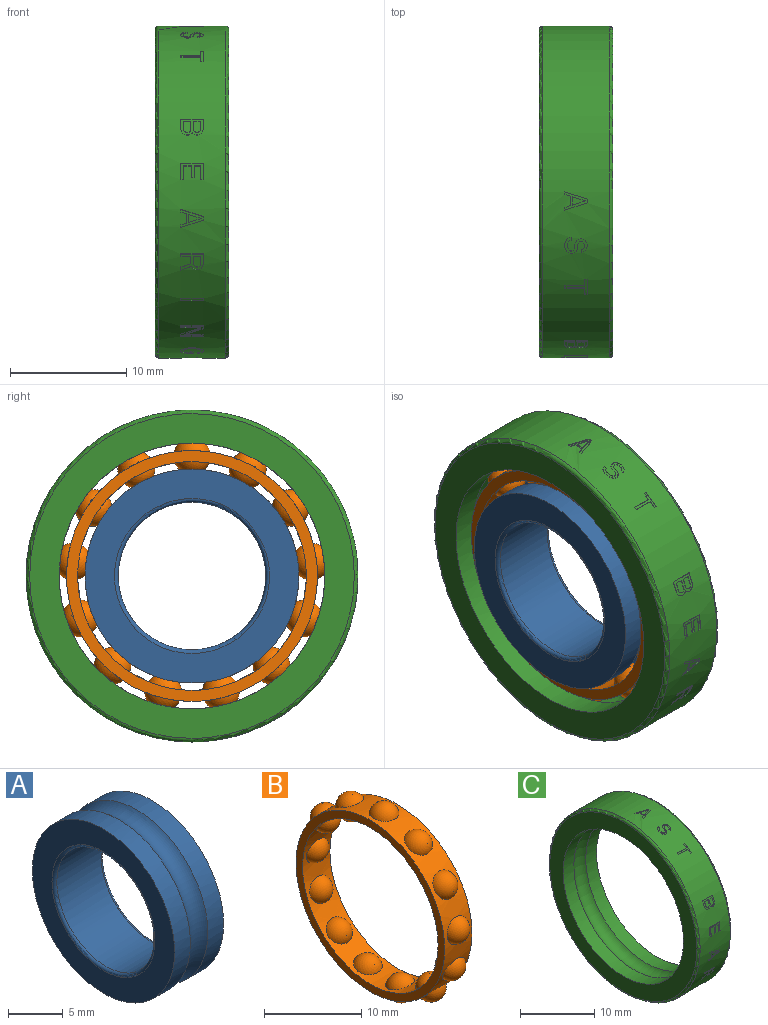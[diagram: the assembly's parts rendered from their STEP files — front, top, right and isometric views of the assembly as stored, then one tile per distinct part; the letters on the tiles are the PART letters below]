
ASSEMBLY  parts=3 mates=2
PART A: 8 faces, bbox 6.4x22.3x22.3 mm
  f0: torus R=10.32mm, axis (1,0,0), area 141.1mm2, adj f1,f2
  f1: cylinder r=9.21mm len=18.42mm, axis (1,0,0), area 118.1mm2, adj f0,f3
  f2: cylinder r=9.21mm len=18.42mm, axis (1,0,0), area 118.1mm2, adj f0,f4
  f3: plane 18.45x18.42mm, normal (-1,0,0), area 126.7mm2, adj f1,f5
  f4: plane 18.45x18.42mm, normal (1,0,0), area 126.7mm2, adj f2,f6
  f5: torus R=6.67mm, axis (1,0,0), area 20.3mm2, adj f3,f7
  f6: torus R=6.67mm, axis (1,0,0), area 20.3mm2, adj f4,f7
  f7: cylinder r=6.35mm len=12.7mm, axis (1,0,0), area 228mm2, adj f5,f6
PART B: 30 faces, bbox 4x23.7x23.5 mm
  f0: sphere r=1.59mm, area 11.9mm2, adj f13
  f1: sphere r=1.59mm, area 11.9mm2, adj f13
  f2: sphere r=1.59mm, area 12.1mm2, adj f13
  f3: sphere r=1.59mm, area 11.9mm2, adj f13
  f4: sphere r=1.59mm, area 12.1mm2, adj f13
  f5: sphere r=1.59mm, area 12.1mm2, adj f13
  f6: sphere r=1.59mm, area 14.4mm2, adj f13
  f7: sphere r=1.59mm, area 12.1mm2, adj f13
  f8: sphere r=1.59mm, area 11.9mm2, adj f13
  f9: sphere r=1.59mm, area 12.1mm2, adj f13
  f10: sphere r=1.59mm, area 12.1mm2, adj f13
  f11: sphere r=1.59mm, area 11.9mm2, adj f13
  f12: sphere r=1.59mm, area 11.5mm2, adj f13
  f13: cylinder r=10.79mm len=21.59mm, axis (1,0,0), area 173.7mm2, adj f0,f1,f2,f3,f4,f5,f6,f7
  f14: sphere r=1.59mm, area 10.5mm2, adj f28
  f15: sphere r=1.59mm, area 10.5mm2, adj f28
  f16: sphere r=1.59mm, area 10.5mm2, adj f28
  f17: sphere r=1.59mm, area 10.5mm2, adj f28
  f18: sphere r=1.59mm, area 10.5mm2, adj f28
  f19: sphere r=1.59mm, area 10.5mm2, adj f28
  f20: plane 21.61x21.59mm, normal (-1,0,0), area 61.8mm2, adj f13,f28
  f21: plane 21.61x21.59mm, normal (1,0,0), area 61.8mm2, adj f13,f28
  f22: sphere r=1.59mm, area 10.5mm2, adj f28
  f23: sphere r=1.59mm, area 10.5mm2, adj f28
  f24: sphere r=1.59mm, area 10.5mm2, adj f28
  f25: sphere r=1.59mm, area 10.5mm2, adj f28
  f26: sphere r=1.59mm, area 10.5mm2, adj f28
  f27: sphere r=1.59mm, area 10.5mm2, adj f28
  f28: cylinder r=9.84mm len=19.69mm, axis (1,0,0), area 153.1mm2, adj f14,f15,f16,f17,f18,f19,f20,f21
  f29: sphere r=1.59mm, area 10.5mm2, adj f28
PART C: 297 faces, bbox 6.4x30.9x30.9 mm
  f0: cylinder r=14.29mm len=1.09mm, axis (1,0,0), area 0.4mm2, adj f5,f6,f7
  f1: cylinder r=14.29mm len=0.91mm, axis (1,0,0), area 0.5mm2, adj f8,f9,f10,f11,f12,f13,f14,f15
  f2: cylinder r=14.29mm len=0.91mm, axis (1,0,0), area 0.6mm2, adj f18,f19,f20,f21,f22,f23,f24,f25
  f3: cylinder r=14.29mm len=1.09mm, axis (1,0,0), area 0.4mm2, adj f28,f29,f30
  f4: cylinder r=14.29mm len=0.9mm, axis (1,0,0), area 0.6mm2, adj f31,f32,f33,f34,f35,f36,f37,f38
  f5: plane 0.71x0.09mm, normal (-1,0,0), area 0mm2, adj f0,f6,f7,f41
  f6: plane 1.09x0.36mm, normal (0.31,0.95,0), area 0.1mm2, adj f0,f5,f7,f41
  f7: plane 1.09x0.36mm, normal (0.31,-0.95,0), area 0.1mm2, adj f0,f5,f6,f41
  f8: plane 0.13x0.09mm, normal (0.95,-0.14,-0.29), area 0mm2, adj f1,f9,f17,f45
  f9: plane 0.1x0.08mm, normal (0.7,-0.31,-0.64), area 0mm2, adj f1,f8,f10,f45
  f10: plane 0.12x0.06mm, normal (0.31,-0.42,-0.85), area 0mm2, adj f1,f9,f11,f45
  f11: plane 0.08x0.05mm, normal (0,-0.44,-0.9), area 0mm2, adj f1,f10,f12,f45
  f12: plane 0.12x0.06mm, normal (-0.31,-0.42,-0.85), area 0mm2, adj f1,f11,f13,f45
  f13: plane 0.1x0.08mm, normal (-0.7,-0.31,-0.64), area 0mm2, adj f1,f12,f14,f45
  f14: plane 0.13x0.09mm, normal (-0.95,-0.14,-0.29), area 0mm2, adj f1,f13,f15,f45
  f15: plane 0.71x0.35mm, normal (-1,0,0), area 0mm2, adj f1,f14,f16,f45
  f16: plane 0.57x0.05mm, normal (0,0.44,0.9), area 0mm2, adj f1,f15,f17,f45
  f17: plane 0.71x0.35mm, normal (1,0,0), area 0mm2, adj f1,f8,f16,f45
  f18: plane 0.12x0.06mm, normal (-0.31,-0.42,-0.85), area 0mm2, adj f2,f19,f27,f45
  f19: plane 0.1x0.08mm, normal (-0.7,-0.31,-0.64), area 0mm2, adj f2,f18,f20,f45
  f20: plane 0.13x0.09mm, normal (-0.95,-0.14,-0.29), area 0mm2, adj f2,f19,f21,f45
  f21: plane 0.71x0.35mm, normal (-1,0,0), area 0mm2, adj f2,f20,f22,f45
  f22: plane 0.61x0.05mm, normal (0,0.44,0.9), area 0mm2, adj f2,f21,f23,f45
  f23: plane 0.71x0.35mm, normal (1,0,0), area 0mm2, adj f2,f22,f24,f45
  f24: plane 0.13x0.09mm, normal (0.95,-0.14,-0.29), area 0mm2, adj f2,f23,f25,f45
  f25: plane 0.1x0.08mm, normal (0.7,-0.31,-0.64), area 0mm2, adj f2,f24,f26,f45
  f26: plane 0.12x0.06mm, normal (0.31,-0.42,-0.85), area 0mm2, adj f2,f25,f27,f45
  f27: plane 0.12x0.05mm, normal (0,-0.44,-0.9), area 0mm2, adj f2,f18,f26,f45
  f28: plane 0.71x0.17mm, normal (-1,0,0), area 0mm2, adj f3,f29,f30,f47
  f29: plane 1.09x0.36mm, normal (0.31,-0.1,0.95), area 0.1mm2, adj f3,f28,f30,f47
  f30: plane 1.09x0.36mm, normal (0.31,0.1,-0.95), area 0.1mm2, adj f3,f28,f29,f47
  f31: plane 0.61x0.05mm, normal (0,-0.37,0.93), area 0mm2, adj f4,f32,f40,f48
  f32: plane 0.71x0.36mm, normal (1,0,0), area 0mm2, adj f4,f31,f33,f48
  f33: plane 0.13x0.1mm, normal (0.95,0.12,-0.3), area 0mm2, adj f4,f32,f34,f48
  f34: plane 0.09x0.08mm, normal (0.7,0.27,-0.66), area 0mm2, adj f4,f33,f35,f48
  f35: plane 0.12x0.07mm, normal (0.31,0.36,-0.88), area 0mm2, adj f4,f34,f36,f48
  f36: plane 0.12x0.05mm, normal (0,0.37,-0.93), area 0mm2, adj f4,f35,f37,f48
  f37: plane 0.12x0.07mm, normal (-0.31,0.36,-0.88), area 0mm2, adj f4,f36,f38,f48
  f38: plane 0.09x0.08mm, normal (-0.7,0.27,-0.66), area 0mm2, adj f4,f37,f39,f48
  f39: plane 0.13x0.1mm, normal (-0.95,0.12,-0.3), area 0mm2, adj f4,f38,f40,f48
  f40: plane 0.71x0.36mm, normal (-1,0,0), area 0mm2, adj f4,f31,f39,f48
  f41: cylinder r=14.24mm len=1.91mm, axis (-1,0,0), area 1mm2, adj f5,f6,f7,f88,f89,f90,f91,f92
  f42: cylinder r=14.24mm len=1.91mm, axis (-1,0,0), area 1.1mm2, adj f52,f53,f54,f55,f56,f57,f58,f59
  f43: cylinder r=14.24mm len=1.91mm, axis (-1,0,0), area 1.1mm2, adj f115,f116,f117,f118,f119,f120,f121,f122
  f44: cylinder r=14.24mm len=1.91mm, axis (-1,0,0), area 0.7mm2, adj f169,f170,f171,f172,f173,f174,f175,f176
  f45: cylinder r=14.24mm len=1.91mm, axis (-1,0,0), area 1.5mm2, adj f8,f9,f10,f11,f12,f13,f14,f15
  f46: cylinder r=14.24mm len=1.91mm, axis (-1,0,0), area 1.3mm2, adj f196,f197,f198,f199,f200,f201,f202,f203
  f47: cylinder r=14.24mm len=1.91mm, axis (-1,0,0), area 1mm2, adj f28,f29,f30,f208,f209,f210,f211,f212
  f48: cylinder r=14.24mm len=1.91mm, axis (-1,0,0), area 1.3mm2, adj f31,f32,f33,f34,f35,f36,f37,f38
  f49: cylinder r=14.24mm len=1.91mm, axis (-1,0,0), area 0.5mm2, adj f232,f233,f234,f235
  f50: cylinder r=14.24mm len=1.91mm, axis (-1,0,0), area 1.4mm2, adj f236,f237,f238,f239,f240,f241,f242,f243
  f51: cylinder r=14.24mm len=1.91mm, axis (-1,0,0), area 1.2mm2, adj f246,f247,f248,f249,f250,f251,f252,f253
  f52: plane 0.16x0.08mm, normal (-0.89,-0.45,0.03), area 0mm2, adj f42,f53,f75,f291
  f53: plane 0.16x0.16mm, normal (-0.7,-0.71,0.05), area 0mm2, adj f42,f52,f54,f291
  f54: plane 0.16x0.08mm, normal (-0.44,-0.9,0.06), area 0mm2, adj f42,f53,f55,f291
  f55: plane 0.2x0.05mm, normal (0,-1,0.07), area 0mm2, adj f42,f54,f56,f291
  f56: plane 0.16x0.08mm, normal (0.44,-0.9,0.06), area 0mm2, adj f42,f55,f57,f291
  f57: plane 0.16x0.16mm, normal (0.7,-0.71,0.05), area 0mm2, adj f42,f56,f58,f291
  f58: plane 0.16x0.08mm, normal (0.89,-0.45,0.03), area 0mm2, adj f42,f57,f97,f291
  f59: plane 0.16x0.12mm, normal (-0.79,-0.61,0.04), area 0mm2, adj f42,f60,f87,f291
  f60: plane 0.16x0.12mm, normal (-0.59,-0.8,0.06), area 0mm2, adj f42,f59,f61,f291
  f61: plane 0.12x0.05mm, normal (-0.31,-0.95,0.07), area 0mm2, adj f42,f60,f62,f291
  f62: plane 0.24x0.06mm, normal (1,0,0), area 0mm2, adj f42,f61,f63,f291
  f63: plane 0.08x0.05mm, normal (0.44,0.9,-0.06), area 0mm2, adj f42,f62,f64,f291
  f64: plane 0.08x0.08mm, normal (0.7,0.71,-0.05), area 0mm2, adj f42,f63,f65,f291
  f65: plane 0.12x0.05mm, normal (0.95,0.32,-0.02), area 0mm2, adj f42,f64,f66,f291
  f66: plane 0.24x0.05mm, normal (1,0,0), area 0mm2, adj f42,f65,f67,f291
  f67: plane 0.12x0.05mm, normal (0.95,-0.32,0.02), area 0mm2, adj f42,f66,f68,f291
  f68: plane 0.12x0.08mm, normal (0.83,-0.56,0.04), area 0mm2, adj f42,f67,f69,f291
  f69: plane 0.12x0.05mm, normal (0.31,-0.95,0.07), area 0mm2, adj f42,f68,f70,f291
  f70: plane 0.08x0.05mm, normal (0,-1,0.07), area 0mm2, adj f42,f69,f71,f291
  f71: plane 0.12x0.05mm, normal (-0.31,-0.95,0.07), area 0mm2, adj f42,f70,f72,f291
  f72: plane 0.12x0.08mm, normal (-0.83,-0.56,0.04), area 0mm2, adj f42,f71,f73,f291
  f73: plane 0.12x0.05mm, normal (-0.95,-0.32,0.02), area 0mm2, adj f42,f72,f74,f291
  f74: plane 0.24x0.05mm, normal (-1,0,0), area 0mm2, adj f42,f73,f75,f291
  f75: plane 0.2x0.05mm, normal (-0.98,-0.2,0.01), area 0mm2, adj f42,f52,f74,f291
  f76: plane 0.24x0.05mm, normal (1,0,0), area 0mm2, adj f42,f77,f114,f291
  f77: plane 0.16x0.06mm, normal (0.97,0.25,-0.02), area 0mm2, adj f42,f76,f78,f291
  f78: plane 0.16x0.08mm, normal (0.89,0.45,-0.03), area 0mm2, adj f42,f77,f79,f291
  f79: plane 0.16x0.16mm, normal (0.7,0.71,-0.05), area 0mm2, adj f42,f78,f80,f291
  f80: plane 0.16x0.05mm, normal (0.24,0.97,-0.07), area 0mm2, adj f42,f79,f81,f291
  f81: plane 0.16x0.05mm, normal (0,1,-0.07), area 0mm2, adj f42,f80,f82,f291
  f82: plane 0.16x0.05mm, normal (-0.24,0.97,-0.07), area 0mm2, adj f42,f81,f83,f291
  f83: plane 0.16x0.16mm, normal (-0.7,0.71,-0.05), area 0mm2, adj f42,f82,f84,f291
  f84: plane 0.16x0.08mm, normal (-0.89,0.45,-0.03), area 0mm2, adj f42,f83,f85,f291
  f85: plane 0.16x0.06mm, normal (-0.97,0.25,-0.02), area 0mm2, adj f42,f84,f86,f291
  f86: plane 0.2x0.05mm, normal (-1,0,0), area 0mm2, adj f42,f85,f87,f291
  f87: plane 0.2x0.05mm, normal (-0.98,-0.2,0.01), area 0mm2, adj f42,f59,f86,f291
  f88: plane 1.91x0.64mm, normal (-0.32,-0.95,0), area 0.1mm2, adj f41,f89,f95,f291
  f89: plane 0.32x0.07mm, normal (-1,0,0), area 0mm2, adj f41,f88,f90,f291
  f90: plane 1.91x0.64mm, normal (-0.32,0.95,0), area 0.1mm2, adj f41,f89,f91,f291
  f91: plane 0.24x0.08mm, normal (1,0,0), area 0mm2, adj f41,f90,f92,f291
  f92: plane 0.49x0.16mm, normal (0.31,-0.95,0), area 0mm2, adj f41,f91,f93,f291
  f93: plane 0.79x0.1mm, normal (1,0,0), area 0mm2, adj f41,f92,f94,f291
  f94: plane 0.49x0.16mm, normal (0.31,0.95,0), area 0mm2, adj f41,f93,f95,f291
  f95: plane 0.24x0.05mm, normal (1,0,0), area 0mm2, adj f41,f88,f94,f291
  f96: torus R=13.97mm, axis (1,0,0), area 44.4mm2, adj f290,f291
  f97: plane 0.2x0.05mm, normal (0.98,-0.2,0.01), area 0mm2, adj f42,f58,f98,f291
  f98: plane 0.32x0.06mm, normal (1,0,0), area 0mm2, adj f42,f97,f99,f291
  f99: plane 0.2x0.06mm, normal (0.98,0.2,-0.01), area 0mm2, adj f42,f98,f100,f291
  f100: plane 0.2x0.12mm, normal (0.85,0.52,-0.04), area 0mm2, adj f42,f99,f101,f291
  f101: plane 0.2x0.12mm, normal (0.51,0.86,-0.06), area 0mm2, adj f42,f100,f102,f291
  f102: plane 0.16x0.05mm, normal (0.24,0.97,-0.07), area 0mm2, adj f42,f101,f103,f291
  f103: plane 0.24x0.07mm, normal (-1,0,0), area 0mm2, adj f42,f102,f104,f291
  f104: plane 0.12x0.05mm, normal (-0.31,-0.95,0.07), area 0mm2, adj f42,f103,f105,f291
  f105: plane 0.12x0.12mm, normal (-0.7,-0.71,0.05), area 0mm2, adj f42,f104,f106,f291
  f106: plane 0.16x0.06mm, normal (-0.97,-0.25,0.02), area 0mm2, adj f42,f105,f107,f291
  f107: plane 0.32x0.06mm, normal (-1,0,0), area 0mm2, adj f42,f106,f108,f291
  f108: plane 0.16x0.05mm, normal (-0.97,0.25,-0.02), area 0mm2, adj f42,f107,f109,f291
  f109: plane 0.12x0.08mm, normal (-0.83,0.56,-0.04), area 0mm2, adj f42,f108,f110,f291
  f110: plane 0.12x0.08mm, normal (-0.55,0.84,-0.06), area 0mm2, adj f42,f109,f111,f291
  f111: plane 0.12x0.05mm, normal (0,1,-0.07), area 0mm2, adj f42,f110,f112,f291
  f112: plane 0.12x0.08mm, normal (0.55,0.84,-0.06), area 0mm2, adj f42,f111,f113,f291
  f113: plane 0.12x0.08mm, normal (0.83,0.56,-0.04), area 0mm2, adj f42,f112,f114,f291
  f114: plane 0.16x0.05mm, normal (0.97,0.25,-0.02), area 0mm2, adj f42,f76,f113,f291
  f115: plane 0.17x0.1mm, normal (-0.97,-0.24,-0.07), area 0mm2, adj f43,f116,f168,f291
  f116: plane 0.2x0.11mm, normal (-1,0,0), area 0mm2, adj f43,f115,f117,f291
  f117: plane 0.2x0.12mm, normal (-0.98,0.19,0.06), area 0mm2, adj f43,f116,f118,f291
  f118: plane 0.16x0.12mm, normal (-0.79,0.58,0.17), area 0mm2, adj f43,f117,f119,f291
  f119: plane 0.16x0.13mm, normal (-0.59,0.77,0.22), area 0mm2, adj f43,f118,f120,f291
  f120: plane 0.12x0.06mm, normal (-0.31,0.91,0.26), area 0mm2, adj f43,f119,f121,f291
  f121: plane 0.24x0.13mm, normal (1,0,0), area 0mm2, adj f43,f120,f122,f291
  f122: plane 0.08x0.06mm, normal (0.44,-0.86,-0.25), area 0mm2, adj f43,f121,f123,f291
  f123: plane 0.09x0.08mm, normal (0.7,-0.69,-0.2), area 0mm2, adj f43,f122,f124,f291
  f124: plane 0.13x0.09mm, normal (0.95,-0.31,-0.09), area 0mm2, adj f43,f123,f125,f291
  f125: plane 0.24x0.13mm, normal (1,0,0), area 0mm2, adj f43,f124,f126,f291
  f126: plane 0.13x0.09mm, normal (0.95,0.31,0.09), area 0mm2, adj f43,f125,f127,f291
  f127: plane 0.13x0.09mm, normal (0.83,0.54,0.16), area 0mm2, adj f43,f126,f128,f291
  f128: plane 0.12x0.06mm, normal (0.31,0.91,0.26), area 0mm2, adj f43,f127,f129,f291
  f129: plane 0.08x0.05mm, normal (0,0.96,0.28), area 0mm2, adj f43,f128,f130,f291
  f130: plane 0.12x0.06mm, normal (-0.31,0.91,0.26), area 0mm2, adj f43,f129,f131,f291
  f131: plane 0.13x0.09mm, normal (-0.83,0.54,0.16), area 0mm2, adj f43,f130,f132,f291
  f132: plane 0.13x0.09mm, normal (-0.95,0.31,0.09), area 0mm2, adj f43,f131,f133,f291
  f133: plane 0.24x0.13mm, normal (-1,0,0), area 0mm2, adj f43,f132,f134,f291
  f134: plane 0.2x0.12mm, normal (-0.98,0.19,0.06), area 0mm2, adj f43,f133,f135,f291
  f135: plane 0.16x0.11mm, normal (-0.89,0.44,0.13), area 0mm2, adj f43,f134,f136,f291
  f136: plane 0.16x0.16mm, normal (-0.7,0.69,0.2), area 0mm2, adj f43,f135,f137,f291
  f137: plane 0.16x0.09mm, normal (-0.44,0.86,0.25), area 0mm2, adj f43,f136,f138,f291
  f138: plane 0.2x0.05mm, normal (0,0.96,0.28), area 0mm2, adj f43,f137,f139,f291
  f139: plane 0.16x0.09mm, normal (0.44,0.86,0.25), area 0mm2, adj f43,f138,f140,f291
  f140: plane 0.16x0.16mm, normal (0.7,0.69,0.2), area 0mm2, adj f43,f139,f141,f291
  f141: plane 0.16x0.11mm, normal (0.89,0.44,0.13), area 0mm2, adj f43,f140,f142,f291
  f142: plane 0.2x0.12mm, normal (0.98,0.19,0.06), area 0mm2, adj f43,f141,f143,f291
  f143: plane 0.32x0.15mm, normal (1,0,0), area 0mm2, adj f43,f142,f144,f291
  f144: plane 0.2x0.11mm, normal (0.98,-0.19,-0.06), area 0mm2, adj f43,f143,f145,f291
  f145: plane 0.2x0.12mm, normal (0.85,-0.5,-0.14), area 0mm2, adj f43,f144,f146,f291
  f146: plane 0.2x0.13mm, normal (0.51,-0.83,-0.24), area 0mm2, adj f43,f145,f147,f291
  f147: plane 0.16x0.06mm, normal (0.24,-0.93,-0.27), area 0mm2, adj f43,f146,f148,f291
  f148: plane 0.24x0.12mm, normal (-1,0,0), area 0mm2, adj f43,f147,f149,f291
  f149: plane 0.12x0.06mm, normal (-0.31,0.91,0.26), area 0mm2, adj f43,f148,f150,f291
  f150: plane 0.13x0.12mm, normal (-0.7,0.69,0.2), area 0mm2, adj f43,f149,f151,f291
  f151: plane 0.17x0.1mm, normal (-0.97,0.24,0.07), area 0mm2, adj f43,f150,f152,f291
  f152: plane 0.32x0.15mm, normal (-1,0,0), area 0mm2, adj f43,f151,f153,f291
  f153: plane 0.16x0.1mm, normal (-0.97,-0.24,-0.07), area 0mm2, adj f43,f152,f154,f291
  f154: plane 0.13x0.09mm, normal (-0.83,-0.54,-0.16), area 0mm2, adj f43,f153,f155,f291
  f155: plane 0.12x0.09mm, normal (-0.55,-0.8,-0.23), area 0mm2, adj f43,f154,f156,f291
  f156: plane 0.12x0.05mm, normal (0,-0.96,-0.28), area 0mm2, adj f43,f155,f157,f291
  f157: plane 0.12x0.09mm, normal (0.55,-0.8,-0.23), area 0mm2, adj f43,f156,f158,f291
  f158: plane 0.13x0.09mm, normal (0.83,-0.54,-0.16), area 0mm2, adj f43,f157,f159,f291
  f159: plane 0.16x0.1mm, normal (0.97,-0.24,-0.07), area 0mm2, adj f43,f158,f160,f291
  f160: plane 0.24x0.13mm, normal (1,0,0), area 0mm2, adj f43,f159,f161,f291
  f161: plane 0.17x0.1mm, normal (0.97,-0.24,-0.07), area 0mm2, adj f43,f160,f162,f291
  f162: plane 0.17x0.1mm, normal (0.89,-0.44,-0.13), area 0mm2, adj f43,f161,f163,f291
  f163: plane 0.17x0.16mm, normal (0.7,-0.69,-0.2), area 0mm2, adj f43,f162,f164,f291
  f164: plane 0.16x0.06mm, normal (0.24,-0.93,-0.27), area 0mm2, adj f43,f163,f165,f291
  f165: plane 0.16x0.05mm, normal (0,-0.96,-0.28), area 0mm2, adj f43,f164,f166,f291
  f166: plane 0.16x0.06mm, normal (-0.24,-0.93,-0.27), area 0mm2, adj f43,f165,f167,f291
  f167: plane 0.17x0.16mm, normal (-0.7,-0.69,-0.2), area 0mm2, adj f43,f166,f168,f291
  f168: plane 0.17x0.1mm, normal (-0.89,-0.44,-0.13), area 0mm2, adj f43,f115,f167,f291
  f169: plane 0.2x0.04mm, normal (0,0.85,0.53), area 0mm2, adj f44,f170,f176,f291
  f170: plane 0.54x0.43mm, normal (1,0,0), area 0mm2, adj f44,f169,f171,f291
  f171: plane 1.7x0.04mm, normal (0,0.85,0.53), area 0.1mm2, adj f44,f170,f172,f291
  f172: plane 0.22x0.18mm, normal (1,0,0), area 0mm2, adj f44,f171,f173,f291
  f173: plane 1.7x0.04mm, normal (0,-0.85,-0.53), area 0.1mm2, adj f44,f172,f174,f291
  f174: plane 0.56x0.39mm, normal (1,0,0), area 0mm2, adj f44,f173,f175,f291
  f175: plane 0.2x0.04mm, normal (0,-0.85,-0.53), area 0mm2, adj f44,f174,f176,f291
  f176: plane 1.26x0.91mm, normal (-1,0,0), area 0.1mm2, adj f44,f169,f175,f291
  f177: plane 0.89x0.43mm, normal (1,0,0), area 0mm2, adj f45,f178,f195,f291
  f178: plane 1.91x0.05mm, normal (0,-0.44,-0.9), area 0.1mm2, adj f45,f177,f179,f291
  f179: plane 0.89x0.43mm, normal (-1,0,0), area 0mm2, adj f45,f178,f180,f291
  f180: plane 0.21x0.12mm, normal (-0.98,0.09,0.18), area 0mm2, adj f45,f179,f181,f291
  f181: plane 0.17x0.12mm, normal (-0.79,0.27,0.55), area 0mm2, adj f45,f180,f182,f291
  f182: plane 0.16x0.13mm, normal (-0.59,0.35,0.72), area 0mm2, adj f45,f181,f183,f291
  f183: plane 0.12x0.06mm, normal (-0.31,0.42,0.85), area 0mm2, adj f45,f182,f184,f291
  f184: plane 0.16x0.05mm, normal (0,0.44,0.9), area 0mm2, adj f45,f183,f185,f291
  f185: plane 0.12x0.06mm, normal (0.31,0.42,0.85), area 0mm2, adj f45,f184,f186,f291
  f186: plane 0.16x0.13mm, normal (0.59,0.35,0.72), area 0mm2, adj f45,f185,f187,f291
  f187: plane 0.1x0.07mm, normal (0.89,0.2,0.41), area 0mm2, adj f45,f186,f188,f291
  f188: plane 0.1x0.07mm, normal (-0.89,0.2,0.41), area 0mm2, adj f45,f187,f189,f291
  f189: plane 0.16x0.13mm, normal (-0.59,0.35,0.72), area 0mm2, adj f45,f188,f190,f291
  f190: plane 0.12x0.06mm, normal (-0.31,0.42,0.85), area 0mm2, adj f45,f189,f191,f291
  f191: plane 0.2x0.05mm, normal (0,0.44,0.9), area 0mm2, adj f45,f190,f192,f291
  f192: plane 0.12x0.06mm, normal (0.31,0.42,0.85), area 0mm2, adj f45,f191,f193,f291
  f193: plane 0.16x0.13mm, normal (0.59,0.35,0.72), area 0mm2, adj f45,f192,f194,f291
  f194: plane 0.17x0.12mm, normal (0.79,0.27,0.55), area 0mm2, adj f45,f193,f195,f291
  f195: plane 0.21x0.12mm, normal (0.98,0.09,0.18), area 0mm2, adj f45,f177,f194,f291
  f196: plane 0.24x0.05mm, normal (0,0.17,0.98), area 0mm2, adj f46,f197,f207,f291
  f197: plane 1.03x0.18mm, normal (1,0,0), area 0.1mm2, adj f46,f196,f198,f291
  f198: plane 0.65x0.05mm, normal (0,0.17,0.98), area 0mm2, adj f46,f197,f199,f291
  f199: plane 1.19x0.19mm, normal (-1,0,0), area 0.1mm2, adj f46,f198,f200,f291
  f200: plane 0.24x0.05mm, normal (0,0.17,0.98), area 0mm2, adj f46,f199,f201,f291
  f201: plane 1.43x0.23mm, normal (1,0,0), area 0.1mm2, adj f46,f200,f202,f291
  f202: plane 1.91x0.05mm, normal (0,-0.17,-0.98), area 0.1mm2, adj f46,f201,f203,f291
  f203: plane 1.43x0.23mm, normal (-1,0,0), area 0.1mm2, adj f46,f202,f204,f291
  f204: plane 0.24x0.05mm, normal (0,0.17,0.98), area 0mm2, adj f46,f203,f205,f291
  f205: plane 1.19x0.19mm, normal (1,0,0), area 0.1mm2, adj f46,f204,f206,f291
  f206: plane 0.53x0.05mm, normal (0,0.17,0.98), area 0mm2, adj f46,f205,f207,f291
  f207: plane 1.03x0.18mm, normal (-1,0,0), area 0.1mm2, adj f46,f196,f206,f291
  f208: plane 1.91x0.63mm, normal (-0.32,-0.1,0.94), area 0.1mm2, adj f47,f209,f215,f291
  f209: plane 0.24x0.1mm, normal (1,0,0), area 0mm2, adj f47,f208,f210,f291
  f210: plane 0.49x0.16mm, normal (0.31,0.1,-0.95), area 0mm2, adj f47,f209,f211,f291
  f211: plane 0.79x0.18mm, normal (1,0,0), area 0mm2, adj f47,f210,f212,f291
  f212: plane 0.49x0.16mm, normal (0.31,-0.1,0.95), area 0mm2, adj f47,f211,f213,f291
  f213: plane 0.24x0.08mm, normal (1,0,0), area 0mm2, adj f47,f212,f214,f291
  f214: plane 1.91x0.64mm, normal (-0.32,0.1,-0.94), area 0.1mm2, adj f47,f213,f215,f291
  f215: plane 0.32x0.1mm, normal (-1,0,0), area 0mm2, adj f47,f208,f214,f291
  f216: plane 0.12x0.07mm, normal (0.31,-0.36,0.88), area 0mm2, adj f48,f217,f231,f291
  f217: plane 0.16x0.13mm, normal (0.59,-0.3,0.75), area 0mm2, adj f48,f216,f218,f291
  f218: plane 0.16x0.12mm, normal (0.89,-0.17,0.42), area 0mm2, adj f48,f217,f219,f291
  f219: plane 0.93x0.34mm, normal (-0.36,-0.35,0.87), area 0.1mm2, adj f48,f218,f220,f291
  f220: plane 0.27x0.18mm, normal (1,0,0), area 0mm2, adj f48,f219,f221,f291
  f221: plane 0.85x0.3mm, normal (0.35,0.35,-0.87), area 0mm2, adj f48,f220,f222,f291
  f222: plane 0.63x0.33mm, normal (1,0,0), area 0mm2, adj f48,f221,f223,f291
  f223: plane 0.85x0.05mm, normal (0,-0.37,0.93), area 0mm2, adj f48,f222,f224,f291
  f224: plane 0.24x0.14mm, normal (1,0,0), area 0mm2, adj f48,f223,f225,f291
  f225: plane 1.91x0.05mm, normal (0,0.37,-0.93), area 0.1mm2, adj f48,f224,f226,f291
  f226: plane 0.89x0.43mm, normal (-1,0,0), area 0mm2, adj f48,f225,f227,f291
  f227: plane 0.2x0.14mm, normal (-0.98,-0.07,0.19), area 0mm2, adj f48,f226,f228,f291
  f228: plane 0.16x0.12mm, normal (-0.79,-0.23,0.56), area 0mm2, adj f48,f227,f229,f291
  f229: plane 0.16x0.13mm, normal (-0.59,-0.3,0.75), area 0mm2, adj f48,f228,f230,f291
  f230: plane 0.12x0.07mm, normal (-0.31,-0.36,0.88), area 0mm2, adj f48,f229,f231,f291
  f231: plane 0.16x0.05mm, normal (0,-0.37,0.93), area 0mm2, adj f48,f216,f230,f291
  f232: plane 0.21x0.19mm, normal (1,0,0), area 0mm2, adj f49,f233,f235,f291
  f233: plane 1.91x0.04mm, normal (0,0.64,-0.77), area 0.1mm2, adj f49,f232,f234,f291
  f234: plane 0.21x0.19mm, normal (-1,0,0), area 0mm2, adj f49,f233,f235,f291
  f235: plane 1.91x0.04mm, normal (0,-0.64,0.77), area 0.1mm2, adj f49,f232,f234,f291
  f236: plane 1.66x0.86mm, normal (0.51,0.69,-0.5), area 0.1mm2, adj f50,f237,f245,f291
  f237: plane 1.66x0.04mm, normal (0,-0.81,0.59), area 0.1mm2, adj f50,f236,f238,f291
  f238: plane 0.22x0.18mm, normal (1,0,0), area 0mm2, adj f50,f237,f239,f291
  f239: plane 1.91x0.04mm, normal (0,0.81,-0.59), area 0.1mm2, adj f50,f238,f240,f291
  f240: plane 0.32x0.25mm, normal (-1,0,0), area 0mm2, adj f50,f239,f241,f291
  f241: plane 1.62x0.87mm, normal (-0.52,-0.69,0.5), area 0.1mm2, adj f50,f240,f242,f291
  f242: plane 1.62x0.04mm, normal (0,0.81,-0.59), area 0.1mm2, adj f50,f241,f243,f291
  f243: plane 0.24x0.16mm, normal (-1,0,0), area 0mm2, adj f50,f242,f244,f291
  f244: plane 1.91x0.04mm, normal (0,-0.81,0.59), area 0.1mm2, adj f50,f243,f245,f291
  f245: plane 0.34x0.22mm, normal (1,0,0), area 0mm2, adj f50,f236,f244,f291
  f246: plane 0.16x0.09mm, normal (0.44,0.84,-0.31), area 0mm2, adj f51,f247,f289,f291
  f247: plane 0.2x0.06mm, normal (0.19,0.92,-0.34), area 0mm2, adj f51,f246,f248,f291
  f248: plane 0.61x0.05mm, normal (0,0.94,-0.34), area 0mm2, adj f51,f247,f249,f291
  f249: plane 0.2x0.06mm, normal (-0.19,0.92,-0.34), area 0mm2, adj f51,f248,f250,f291
  f250: plane 0.16x0.09mm, normal (-0.44,0.84,-0.31), area 0mm2, adj f51,f249,f251,f291
  f251: plane 0.17x0.16mm, normal (-0.7,0.67,-0.24), area 0mm2, adj f51,f250,f252,f291
  f252: plane 0.17x0.1mm, normal (-0.89,0.43,-0.16), area 0mm2, adj f51,f251,f253,f291
  f253: plane 0.21x0.11mm, normal (-0.98,0.19,-0.07), area 0mm2, adj f51,f252,f254,f291
  f254: plane 0.36x0.15mm, normal (-1,0,0), area 0mm2, adj f51,f253,f255,f291
  f255: plane 0.21x0.1mm, normal (-0.98,-0.19,0.07), area 0mm2, adj f51,f254,f256,f291
  f256: plane 0.17x0.09mm, normal (-0.89,-0.43,0.16), area 0mm2, adj f51,f255,f257,f291
  f257: plane 0.17x0.16mm, normal (-0.7,-0.67,0.24), area 0mm2, adj f51,f256,f258,f291
  f258: plane 0.2x0.06mm, normal (-0.19,-0.92,0.34), area 0mm2, adj f51,f257,f259,f291
  f259: plane 0.25x0.11mm, normal (1,0,0), area 0mm2, adj f51,f258,f260,f291
  f260: plane 0.12x0.06mm, normal (0.31,0.89,-0.33), area 0mm2, adj f51,f259,f261,f291
  f261: plane 0.13x0.08mm, normal (0.83,0.53,-0.19), area 0mm2, adj f51,f260,f262,f291
  f262: plane 0.17x0.09mm, normal (0.97,0.23,-0.08), area 0mm2, adj f51,f261,f263,f291
  f263: plane 0.36x0.15mm, normal (1,0,0), area 0mm2, adj f51,f262,f264,f291
  f264: plane 0.17x0.1mm, normal (0.97,-0.23,0.08), area 0mm2, adj f51,f263,f265,f291
  f265: plane 0.13x0.09mm, normal (0.83,-0.53,0.19), area 0mm2, adj f51,f264,f266,f291
  f266: plane 0.12x0.09mm, normal (0.55,-0.79,0.29), area 0mm2, adj f51,f265,f267,f291
  f267: plane 0.16x0.06mm, normal (0.24,-0.91,0.33), area 0mm2, adj f51,f266,f268,f291
  f268: plane 0.61x0.05mm, normal (0,-0.94,0.34), area 0mm2, adj f51,f267,f269,f291
  f269: plane 0.16x0.06mm, normal (-0.24,-0.91,0.33), area 0mm2, adj f51,f268,f270,f291
  f270: plane 0.12x0.09mm, normal (-0.55,-0.79,0.29), area 0mm2, adj f51,f269,f271,f291
  f271: plane 0.13x0.09mm, normal (-0.83,-0.53,0.19), area 0mm2, adj f51,f270,f272,f291
  f272: plane 0.17x0.1mm, normal (-0.97,-0.23,0.08), area 0mm2, adj f51,f271,f273,f291
  f273: plane 0.36x0.15mm, normal (-1,0,0), area 0mm2, adj f51,f272,f274,f291
  f274: plane 0.17x0.09mm, normal (-0.97,0.23,-0.08), area 0mm2, adj f51,f273,f275,f291
  f275: plane 0.13x0.08mm, normal (-0.83,0.53,-0.19), area 0mm2, adj f51,f274,f276,f291
  f276: plane 0.12x0.06mm, normal (-0.31,0.89,-0.33), area 0mm2, adj f51,f275,f277,f291
  f277: plane 0.32x0.05mm, normal (0,0.94,-0.34), area 0mm2, adj f51,f276,f278,f291
  f278: plane 0.36x0.14mm, normal (1,0,0), area 0mm2, adj f51,f277,f279,f291
  f279: plane 0.24x0.05mm, normal (0,0.94,-0.34), area 0mm2, adj f51,f278,f280,f291
  f280: plane 0.59x0.2mm, normal (-1,0,0), area 0mm2, adj f51,f279,f281,f291
  f281: plane 0.61x0.05mm, normal (0,-0.94,0.34), area 0mm2, adj f51,f280,f282,f291
  f282: plane 0.16x0.06mm, normal (0.24,-0.91,0.33), area 0mm2, adj f51,f281,f283,f291
  f283: plane 0.17x0.16mm, normal (0.7,-0.67,0.24), area 0mm2, adj f51,f282,f284,f291
  f284: plane 0.17x0.09mm, normal (0.89,-0.43,0.16), area 0mm2, adj f51,f283,f285,f291
  f285: plane 0.21x0.1mm, normal (0.98,-0.19,0.07), area 0mm2, adj f51,f284,f286,f291
  f286: plane 0.36x0.15mm, normal (1,0,0), area 0mm2, adj f51,f285,f287,f291
  f287: plane 0.21x0.11mm, normal (0.98,0.19,-0.07), area 0mm2, adj f51,f286,f288,f291
  f288: plane 0.17x0.1mm, normal (0.89,0.43,-0.16), area 0mm2, adj f51,f287,f289,f291
  f289: plane 0.17x0.16mm, normal (0.7,0.67,-0.24), area 0mm2, adj f51,f246,f288,f291
  f290: plane 27.96x27.94mm, normal (-1,0,0), area 202.7mm2, adj f96,f292
  f291: cylinder r=14.29mm len=28.58mm, axis (1,0,0), area 498.6mm2, adj f52,f53,f54,f55,f56,f57,f58,f59
  f292: cylinder r=11.43mm len=22.86mm, axis (1,0,0), area 146.6mm2, adj f290,f294
  f293: torus R=13.97mm, axis (1,0,0), area 44.4mm2, adj f291,f295
  f294: torus R=10.32mm, axis (1,0,0), area 186.3mm2, adj f292,f296
  f295: plane 27.96x27.94mm, normal (1,0,0), area 202.7mm2, adj f293,f296
  f296: cylinder r=11.43mm len=22.86mm, axis (1,0,0), area 146.6mm2, adj f294,f295
PLACE A at identity fixed
PLACE B t=(0.05,0,0)mm
PLACE C at identity
MATE fastened C.f0 <-> A.f0  axis (1,0,0) through (3.18,0,0)mm
MATE fastened B.f13 <-> A.f0  axis (1,0,0) through (2.03,0,0)mm
